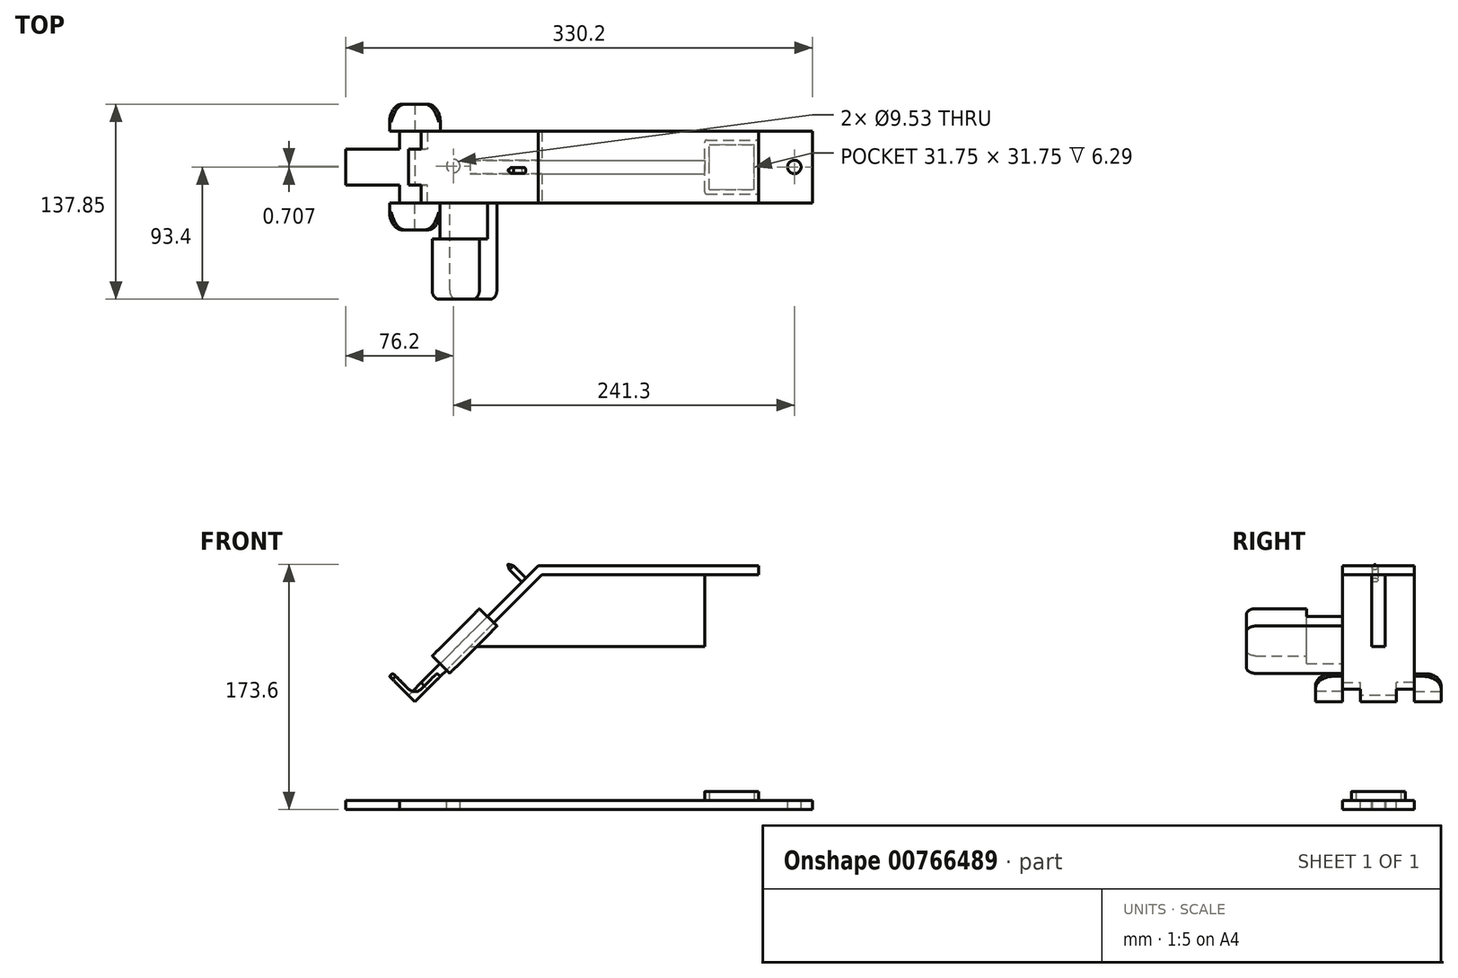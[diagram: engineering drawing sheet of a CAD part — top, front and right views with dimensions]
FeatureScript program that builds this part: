
annotation { "Feature Type Name" : "Feature", "Feature Type Description" : "" }
export const myFeature = defineFeature(function(context is Context, id is Id, definition is map)
    precondition{}
    {
        {
            assignVariable(context, id + "F0", {"name" : "haut", "anyValue" : 8 - 0.49 - 1 - .25 + 0.03});
        }
        {
            var Q0;
            Q0=qCreatedBy(makeId("Top.planeOp"),FACE);
            var sketch = newSketch(context, id + "F1", { "sketchPlane" : qUnion([Q0])});
            skLineSegment(sketch, "E0.bottom", {"start": v(0, 0) * mm, "end": v(114.3, 0) * mm});
            skLineSegment(sketch, "E0.top", {"start": v(0, 50.8) * mm, "end": v(114.3, 50.8) * mm});
            skLineSegment(sketch, "E0.left", {"start": v(0, 0) * mm, "end": v(0, 50.8) * mm});
            skLineSegment(sketch, "E0.right", {"start": v(114.3, 0) * mm, "end": v(114.3, 50.8) * mm});
            skLineSegment(sketch, "E1.bottom", {"start": v(0, 0) * mm, "end": v(-177.8, 0) * mm});
            skLineSegment(sketch, "E1.top", {"start": v(0, 50.8) * mm, "end": v(-177.8, 50.8) * mm});
            skLineSegment(sketch, "E1.right", {"start": v(-215.9, 12.7) * mm, "end": v(-215.9, 38.1) * mm});
            skLineSegment(sketch, "E2.top", {"start": v(-215.9, 38.1) * mm, "end": v(-177.8, 38.1) * mm});
            skLineSegment(sketch, "E2.right", {"start": v(-177.8, 50.8) * mm, "end": v(-177.8, 38.1) * mm});
            skLineSegment(sketch, "E3.top", {"start": v(-215.9, 12.7) * mm, "end": v(-177.8, 12.7) * mm});
            skLineSegment(sketch, "E3.right", {"start": v(-177.8, 0) * mm, "end": v(-177.8, 12.7) * mm});
            skCircle(sketch, "E4", {"center": v(101.6, 25.4) * mm, "radius": 4.76 * mm});
            skCircle(sketch, "E5", {"center": v(-139.7, 26.1) * mm, "radius": 4.76 * mm});
            skSolve(sketch);
        }
        {
            var Q0;
            Q0=qSketchRegion(id+"F1",true);
            extrude(context, id + "F2", {"entities" : qUnion([Q0]), "oppositeDirection" : true, "depth" : 6.35 * mm, "offsetDistance" : 25.4 * mm});
        }
        {
            var Q0;
            Q0=makeQuery(id+"F2.opExtrude","CAP_FACE",FACE,{"disambiguationData":[OSD([sQuery(id+"F1.wireOp",EDGE,"E0.bottom"),sQuery(id+"F1.wireOp",EDGE,"E0.top"),sQuery(id+"F1.wireOp",EDGE,"E0.left"),sQuery(id+"F1.wireOp",EDGE,"E0.right")])],"isStart":true});
            var sketch = newSketch(context, id + "F3", { "sketchPlane" : qUnion([Q0])});
            skLineSegment(sketch, "E6.bottom", {"start": v(38.1, 6.35) * mm, "end": v(76.2, 6.35) * mm});
            skLineSegment(sketch, "E6.top", {"start": v(38.1, 44.45) * mm, "end": v(76.2, 44.45) * mm});
            skLineSegment(sketch, "E6.left", {"start": v(38.1, 6.35) * mm, "end": v(38.1, 44.45) * mm});
            skLineSegment(sketch, "E6.right", {"start": v(76.2, 6.35) * mm, "end": v(76.2, 44.45) * mm});
            skLineSegment(sketch, "E7.0", {"start": v(41.27, 41.28) * mm, "end": v(73.03, 41.28) * mm});
            skLineSegment(sketch, "E7.1", {"start": v(41.27, 9.52) * mm, "end": v(41.27, 41.28) * mm});
            skLineSegment(sketch, "E7.2", {"start": v(41.27, 9.52) * mm, "end": v(73.03, 9.53) * mm});
            skLineSegment(sketch, "E7.3", {"start": v(73.03, 9.53) * mm, "end": v(73.03, 41.28) * mm});
            skSolve(sketch);
        }
        {
            var Q0;
            Q0=qSketchRegion(id+"F3",true);
            extrude(context, id + "F4", {"entities" : qUnion([Q0]), "operationType" : NewBodyOperationType.ADD, "depth" : (getVariable(context, 'haut')) * mm, "offsetDistance" : 25.4 * mm});
        }
        {
            var Q0;
            Q0=makeQuery(id+"F4.opExtrude","SWEPT_FACE",FACE,{"disambiguationData":[OSD([sQuery(id+"F3.wireOp",EDGE,"E6.bottom")])]});
            var sketch = newSketch(context, id + "F5", { "sketchPlane" : qUnion([Q0])});
            skLineSegment(sketch, "E8", {"start": v(76.2, 159.77) * mm, "end": v(-77.04, 159.77) * mm});
            skLineSegment(sketch, "E9", {"start": v(-77.04, 159.77) * mm, "end": v(-166.85, 69.96) * mm});
            skLineSegment(sketch, "E10.0", {"start": v(76.2, 166.12) * mm, "end": v(-79.67, 166.12) * mm});
            skLineSegment(sketch, "E11.0", {"start": v(-79.67, 166.12) * mm, "end": v(-171.34, 74.45) * mm});
            skLineSegment(sketch, "E12", {"start": v(-166.85, 69.96) * mm, "end": v(-171.34, 74.45) * mm});
            skLineSegment(sketch, "E13", {"start": v(76.2, 159.77) * mm, "end": v(76.2, 166.12) * mm});
            skSolve(sketch);
        }
        {
            var Q0;
            Q0=qSketchRegion(id+"F5",true);
            extrude(context, id + "F6", {"entities" : qUnion([Q0]), "operationType" : NewBodyOperationType.ADD, "oppositeDirection" : true, "depth" : 44.45 * mm, "offsetDistance" : 25.4 * mm, "hasSecondDirection" : true, "secondDirectionOppositeDirection" : false, "secondDirectionDepth" : 6.35 * mm});
        }
        {
            var Q0;
            Q0=makeQuery(id+"F6.opExtrude","SWEPT_FACE",FACE,{"disambiguationData":[OSD([sQuery(id+"F5.wireOp",EDGE,"E11.0")])]});
            var sketch = newSketch(context, id + "F7", { "sketchPlane" : qUnion([Q0])});
            skCircle(sketch, "E14", {"center": v(-23.02, 46.84) * mm, "radius": 2.04 * mm});
            skLineSegment(sketch, "E15.direction1", {"start": v(-23.02, 46.84) * mm, "end": v(2.38, 46.84) * mm, "construction": true});
            skLineSegment(sketch, "E15.direction2", {"start": v(-23.02, 46.84) * mm, "end": v(-23.02, -80.16) * mm, "construction": true});
            skSolve(sketch);
        }
        {
            var Q0;
            Q0=qSketchRegion(id+"F7",true);
            extrude(context, id + "F8", {"entities" : qUnion([Q0]), "operationType" : NewBodyOperationType.ADD, "depth" : 15.88 * mm, "offsetDistance" : 25.4 * mm});
        }
        {
            var Q0;
            Q0=makeQuery(id+"F8.opExtrude","CAP_EDGE",EDGE,{"disambiguationData":[OSD([sQuery(id+"F7.wireOp",EDGE,"E14")])],"isStart":false});
            var Q1;
            Q1=makeQuery(id+"F8.opExtrude","CAP_EDGE",EDGE,{"disambiguationData":[OSD([sQuery(id+"F7.wireOp",EDGE,"E15.0.1.0")])],"isStart":false});
            chamfer(context, id + "F9", {"entities" : qUnion([Q0, Q1]), "chamferType" : ChamferType.OFFSET_ANGLE, "width" : 2.03 * mm, "oppositeDirection" : false, "angle" : 60 * degree, "tangentPropagation" : true});
        }
        {
            var Q0;
            Q0=makeQuery(id+"F7.imprint","IMPRINT",FACE,{"disambiguationData":[TD([[makeQuery(id+"F7.imprint","IMPRINT",EDGE,{"derivedFrom":sQuery(id+"F7.wireOp",EDGE,"E14")}),-1.0]])]});
            var sketch = newSketch(context, id + "F10", { "sketchPlane" : qUnion([Q0])});
            skLineSegment(sketch, "E16.bottom", {"start": v(-50.8, -68.5) * mm, "end": v(-38.1, -68.5) * mm});
            skLineSegment(sketch, "E16.top", {"start": v(-50.8, -55.8) * mm, "end": v(-38.1, -55.8) * mm});
            skLineSegment(sketch, "E16.left", {"start": v(-50.8, -68.5) * mm, "end": v(-50.8, -55.8) * mm});
            skLineSegment(sketch, "E16.right", {"start": v(-38.1, -68.5) * mm, "end": v(-38.1, -55.8) * mm});
            skLineSegment(sketch, "E17.bottom", {"start": v(0, -68.5) * mm, "end": v(-12.7, -68.5) * mm});
            skLineSegment(sketch, "E17.top", {"start": v(0, -55.8) * mm, "end": v(-12.7, -55.8) * mm});
            skLineSegment(sketch, "E17.left", {"start": v(0, -68.5) * mm, "end": v(0, -55.8) * mm});
            skLineSegment(sketch, "E17.right", {"start": v(-12.7, -68.5) * mm, "end": v(-12.7, -55.8) * mm});
            skSolve(sketch);
        }
        {
            var Q0;
            Q0=qSketchRegion(id+"F10",true);
            extrude(context, id + "F11", {"entities" : qUnion([Q0]), "operationType" : NewBodyOperationType.REMOVE, "oppositeDirection" : true, "depth" : 25.4 * mm, "offsetDistance" : 25.4 * mm});
        }
        {
            var Q0;
            Q0=makeQuery(id+"F6.opExtrude","CAP_FACE",FACE,{"disambiguationData":[OSD([sQuery(id+"F5.wireOp",EDGE,"E8"),sQuery(id+"F5.wireOp",EDGE,"E9"),sQuery(id+"F5.wireOp",EDGE,"E10.0"),sQuery(id+"F5.wireOp",EDGE,"E11.0"),sQuery(id+"F5.wireOp",EDGE,"E12"),sQuery(id+"F5.wireOp",EDGE,"E13")])],"isStart":false});
            var sketch = newSketch(context, id + "F12", { "sketchPlane" : qUnion([Q0])});
            skLineSegment(sketch, "E18", {"start": v(148.89, 87.92) * mm, "end": v(166.85, 69.96) * mm});
            skLineSegment(sketch, "E19", {"start": v(148.89, 87.92) * mm, "end": v(151.13, 90.17) * mm});
            skLineSegment(sketch, "E20", {"start": v(166.85, 69.96) * mm, "end": v(184.8, 87.92) * mm});
            skLineSegment(sketch, "E21.0", {"start": v(151.13, 90.17) * mm, "end": v(166.85, 74.45) * mm});
            skLineSegment(sketch, "E22.0", {"start": v(166.85, 74.45) * mm, "end": v(182.56, 90.17) * mm});
            skLineSegment(sketch, "E23.0", {"start": v(182.56, 90.17) * mm, "end": v(184.8, 87.92) * mm});
            skSolve(sketch);
        }
        {
            var Q0;
            Q0=qSketchRegion(id+"F12",true);
            extrude(context, id + "F13", {"entities" : qUnion([Q0]), "depth" : 19.05 * mm, "offsetDistance" : 25.4 * mm});
        }
        {
            var Q0;
            Q0=makeQuery(id+"F13.opExtrude","CAP_EDGE",EDGE,{"disambiguationData":[OSD([sQuery(id+"F12.wireOp",EDGE,"E23.0")])],"isStart":false});
            fillet(context, id + "F14", {"entities" : qUnion([Q0]), "radius" : 12.7 * mm, "tangentPropagation" : true, "allowEdgeOverflow" : false});
        }
        {
            var Q0;
            Q0=makeQuery(id+"F13.opExtrude","CAP_EDGE",EDGE,{"disambiguationData":[OSD([sQuery(id+"F12.wireOp",EDGE,"E19")])],"isStart":false});
            fillet(context, id + "F15", {"entities" : qUnion([Q0]), "radius" : 12.7 * mm, "tangentPropagation" : true, "allowEdgeOverflow" : false});
        }
        {
            var Q0;
            Q0=makeQuery(id+"F13.opExtrude","SWEPT_EDGE",EDGE,{"disambiguationData":[OSD([sQuery(id+"F12.wireOp",EDGE,"E21.0"),sQuery(id+"F12.wireOp",EDGE,"E22.0")])]});
            fillet(context, id + "F16", {"entities" : qUnion([Q0]), "radius" : 6.35 * mm, "tangentPropagation" : true, "allowEdgeOverflow" : false});
        }
        {
            var Q0;
            Q0=makeQuery(id+"F13.opExtrude","SWEPT_EDGE",EDGE,{"disambiguationData":[OSD([sQuery(id+"F12.wireOp",EDGE,"E22.0"),sQuery(id+"F12.wireOp",EDGE,"E23.0")])]});
            var Q1;
            Q1=makeQuery(id+"F13.opExtrude","SWEPT_EDGE",EDGE,{"disambiguationData":[OSD([sQuery(id+"F12.wireOp",EDGE,"E19"),sQuery(id+"F12.wireOp",EDGE,"E21.0")])]});
            fillet(context, id + "F17", {"entities" : qUnion([Q0, Q1]), "radius" : 1.59 * mm, "allowEdgeOverflow" : false});
        }
        {
            var Q0;
            Q0=makeQuery(id+"F13.opExtrude","SWEPT_BODY",BODY,{"disambiguationData":[OSD([sQuery(id+"F12.wireOp",EDGE,"E18"),sQuery(id+"F12.wireOp",EDGE,"E19"),sQuery(id+"F12.wireOp",EDGE,"E20"),sQuery(id+"F12.wireOp",EDGE,"E21.0"),sQuery(id+"F12.wireOp",EDGE,"E22.0"),sQuery(id+"F12.wireOp",EDGE,"E23.0")])]});
            var Q1;
            {var subQ0=sQuery(id+"F5.wireOp",EDGE,"E9");Q1=makeQuery(id+"F5.imprint","IMPRINT",FACE,{"disambiguationData":[TD([[makeQuery(id+"F5.imprint","IMPRINT",EDGE,{"derivedFrom":subQ0}),-1.0]])]});}
            mirror(context, id + "F18", {"entities" : qUnion([Q0]), "mirrorPlane" : qUnion([Q1])});
        }
        {
            var Q0;
            Q0=makeQuery(id+"F18.opPattern","COPY",BODY,{"derivedFrom":makeQuery(id+"F13.opExtrude","SWEPT_BODY",BODY,{"disambiguationData":[OSD([sQuery(id+"F12.wireOp",EDGE,"E18"),sQuery(id+"F12.wireOp",EDGE,"E19"),sQuery(id+"F12.wireOp",EDGE,"E20"),sQuery(id+"F12.wireOp",EDGE,"E21.0"),sQuery(id+"F12.wireOp",EDGE,"E22.0"),sQuery(id+"F12.wireOp",EDGE,"E23.0")])]}),"instanceName":"1"});
            var Q1;
            Q1=makeQuery(id+"F18.opPattern","COPY",EDGE,{"derivedFrom":makeQuery(id+"F13.opExtrude","SWEPT_EDGE",EDGE,{"disambiguationData":[OSD([sQuery(id+"F12.wireOp",EDGE,"E18"),sQuery(id+"F12.wireOp",EDGE,"E20")])]}),"instanceName":"1"});
            var Q2;
            Q2=makeQuery(id+"F18.opPattern","COPY",EDGE,{"derivedFrom":makeQuery(id+"F13.opExtrude","SWEPT_EDGE",EDGE,{"disambiguationData":[OSD([sQuery(id+"F12.wireOp",EDGE,"E18"),sQuery(id+"F12.wireOp",EDGE,"E20")])]}),"instanceName":"1"});
            transform(context, id + "F19", {"entities" : qUnion([Q0]), "transformType" : TransformType.TRANSLATION_DISTANCE, "transformDirection" : qUnion([Q2]), "distance" : 38.1 * mm, "makeCopy" : false});
        }
        {
            var Q0;
            Q0=makeQuery(id+"F7.imprint","IMPRINT",FACE,{"disambiguationData":[TD([[makeQuery(id+"F7.imprint","IMPRINT",EDGE,{"derivedFrom":sQuery(id+"F7.wireOp",EDGE,"E14")}),-1.0]])]});
            var sketch = newSketch(context, id + "F20", { "sketchPlane" : qUnion([Q0])});
            skLineSegment(sketch, "E24.bottom", {"start": v(68, -36.92) * mm, "end": v(0, -36.92) * mm});
            skLineSegment(sketch, "E24.top", {"start": v(68, 10.32) * mm, "end": v(0, 10.32) * mm});
            skLineSegment(sketch, "E24.left", {"start": v(68, -36.92) * mm, "end": v(68, 10.32) * mm});
            skLineSegment(sketch, "E24.right", {"start": v(0, -36.92) * mm, "end": v(0, 10.32) * mm});
            skSolve(sketch);
        }
        {
            var Q0;
            Q0 = qSketchRegion(id + "F20", true);
            extrude(context, id + "F21", {"entities" : qUnion([Q0]), "oppositeDirection" : true, "depth" : 9.52 * mm, "offsetDistance" : 25.4 * mm, "hasSecondDirection" : true, "secondDirectionOppositeDirection" : false, "secondDirectionDepth" : 7.94 * mm});
        }
        {
            var Q0;
            Q0=makeQuery(id+"F21.opExtrude","CAP_FACE",FACE,{"disambiguationData":[OSD([sQuery(id+"F20.wireOp",EDGE,"E24.bottom"),sQuery(id+"F20.wireOp",EDGE,"E24.top"),sQuery(id+"F20.wireOp",EDGE,"E24.left"),sQuery(id+"F20.wireOp",EDGE,"E24.right")])],"isStart":true});
            var sketch = newSketch(context, id + "F22", { "sketchPlane" : qUnion([Q0])});
            skLineSegment(sketch, "E25.bottom", {"start": v(0, -36.92) * mm, "end": v(25.4, -36.92) * mm});
            skLineSegment(sketch, "E25.top", {"start": v(0, 10.32) * mm, "end": v(25.4, 10.32) * mm});
            skLineSegment(sketch, "E25.left", {"start": v(0, -36.92) * mm, "end": v(0, 10.32) * mm});
            skLineSegment(sketch, "E25.right", {"start": v(25.4, -36.92) * mm, "end": v(25.4, 10.32) * mm});
            skSolve(sketch);
        }
        {
            var Q0;
            Q0 = qSketchRegion(id + "F22", true);
            extrude(context, id + "F23", {"entities" : qUnion([Q0]), "operationType" : NewBodyOperationType.REMOVE, "oppositeDirection" : true, "depth" : 7.94 * mm, "offsetDistance" : 25.4 * mm});
        }
        {
            var Q0;
            Q0=makeQuery(id+"F4.opExtrude","SWEPT_FACE",FACE,{"disambiguationData":[OSD([sQuery(id+"F3.wireOp",EDGE,"E6.left")])]});
            var sketch = newSketch(context, id + "F24", { "sketchPlane" : qUnion([Q0])});
            skLineSegment(sketch, "E26.0", {"start": v(-30.16, 159.77) * mm, "end": v(-30.16, 108.97) * mm});
            skLineSegment(sketch, "E26.1", {"start": v(-30.16, 159.77) * mm, "end": v(-20.64, 159.77) * mm});
            skLineSegment(sketch, "E26.2", {"start": v(-20.64, 159.77) * mm, "end": v(-20.64, 108.97) * mm});
            skLineSegment(sketch, "E26.3", {"start": v(-30.16, 108.97) * mm, "end": v(-20.64, 108.97) * mm});
            skSolve(sketch);
        }
        {
            var Q0;
            Q0 = qSketchRegion(id + "F24", true);
            var Q1;
            Q1=makeQuery(id+"F6.opExtrude","SWEPT_FACE",FACE,{"disambiguationData":[OSD([sQuery(id+"F5.wireOp",EDGE,"E9")])]});
            extrude(context, id + "F25", {"entities" : qUnion([Q0]), "operationType" : NewBodyOperationType.ADD, "endBound" : BoundingType.UP_TO_SURFACE, "depth" : 115.14 * mm, "endBoundEntityFace" : qUnion([Q1]), "offsetDistance" : 25.4 * mm});
        }
        {
            var Q0;
            Q0=makeQuery(id+"F21.opExtrude","SWEPT_EDGE",EDGE,{"disambiguationData":[OSD([sQuery(id+"F20.wireOp",EDGE,"E24.top"),sQuery(id+"F20.wireOp",EDGE,"E24.left")])]});
            var Q1;
            Q1=makeQuery(id+"F21.opExtrude","SWEPT_EDGE",EDGE,{"disambiguationData":[OSD([sQuery(id+"F20.wireOp",EDGE,"E24.bottom"),sQuery(id+"F20.wireOp",EDGE,"E24.left")])]});
            fillet(context, id + "F26", {"entities" : qUnion([Q0, Q1]), "radius" : 6.35 * mm, "tangentPropagation" : true, "allowEdgeOverflow" : false});
        }
        {
            var Q0;
            Q0=makeQuery(id+"F4.opExtrude","SWEPT_EDGE",EDGE,{"disambiguationData":[OSD([sQuery(id+"F3.wireOp",EDGE,"E6.bottom"),sQuery(id+"F3.wireOp",EDGE,"E6.right")])]});
            var Q1;
            Q1=makeQuery(id+"F4.opExtrude","SWEPT_EDGE",EDGE,{"disambiguationData":[OSD([sQuery(id+"F3.wireOp",EDGE,"E6.bottom"),sQuery(id+"F3.wireOp",EDGE,"E6.left")])]});
            var Q2;
            Q2=makeQuery(id+"F4.opExtrude","SWEPT_EDGE",EDGE,{"disambiguationData":[OSD([sQuery(id+"F3.wireOp",EDGE,"E6.top"),sQuery(id+"F3.wireOp",EDGE,"E6.right")])]});
            var Q3;
            Q3=makeQuery(id+"F4.opExtrude","SWEPT_EDGE",EDGE,{"disambiguationData":[OSD([sQuery(id+"F3.wireOp",EDGE,"E6.top"),sQuery(id+"F3.wireOp",EDGE,"E6.left")])]});
            fillet(context, id + "F27", {"entities" : qUnion([Q0, Q1, Q2, Q3]), "radius" : 1.59 * mm, "tangentPropagation" : true, "allowEdgeOverflow" : false});
        }
    });
